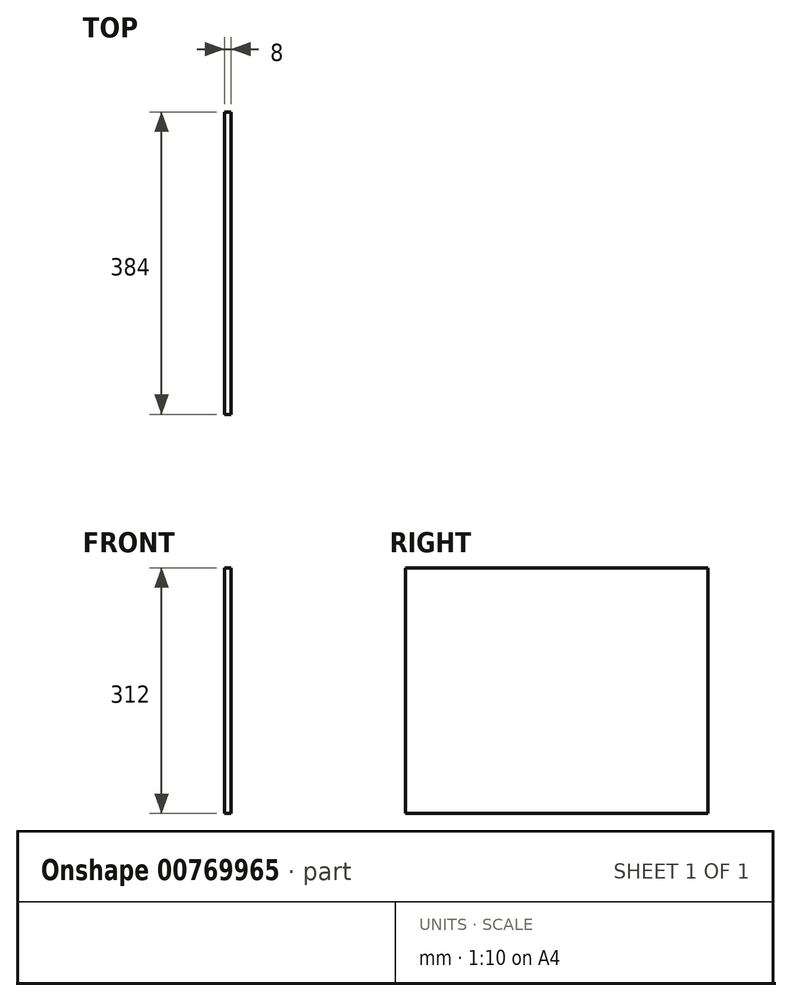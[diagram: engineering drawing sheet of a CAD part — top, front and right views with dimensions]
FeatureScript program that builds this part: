
annotation { "Feature Type Name" : "Feature", "Feature Type Description" : "" }
export const myFeature = defineFeature(function(context is Context, id is Id, definition is map)
    precondition{}
    {
        {
            var Q0;
            Q0=qCreatedBy(makeId("Right.planeOp"),FACE);
            var sketch = newSketch(context, id + "F0", { "sketchPlane" : qUnion([Q0])});
            skLineSegment(sketch, "E0.bottom", {"start": v(192, -156) * mm, "end": v(-192, -156) * mm});
            skLineSegment(sketch, "E0.top", {"start": v(192, 156) * mm, "end": v(-192, 156) * mm});
            skLineSegment(sketch, "E0.left", {"start": v(192, -156) * mm, "end": v(192, 156) * mm});
            skLineSegment(sketch, "E0.right", {"start": v(-192, -156) * mm, "end": v(-192, 156) * mm});
            skPoint(sketch, "E0.middle", {"position": v(0, 0) * mm});
            skSolve(sketch);
        }
        {
            var Q0;
            Q0 = qSketchRegion(id + "F0", true);
            extrude(context, id + "F1", {"entities" : qUnion([Q0]), "depth" : 8 * mm, "offsetDistance" : 25 * mm});
        }
    });
